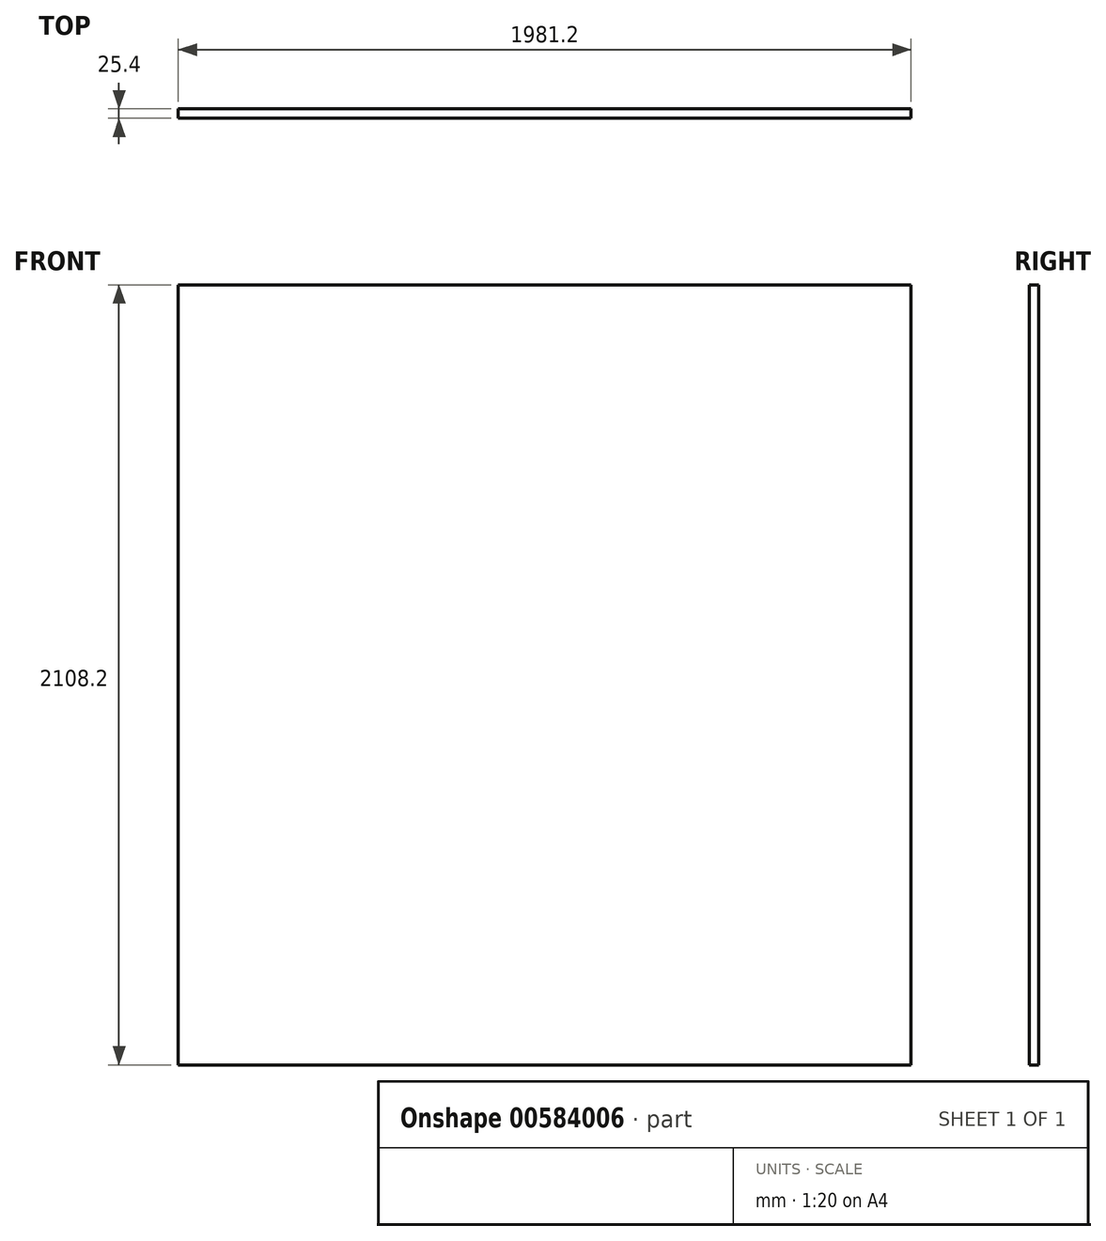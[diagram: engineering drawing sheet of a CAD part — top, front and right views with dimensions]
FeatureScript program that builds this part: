
annotation { "Feature Type Name" : "Feature", "Feature Type Description" : "" }
export const myFeature = defineFeature(function(context is Context, id is Id, definition is map)
    precondition{}
    {
        {
            var Q0;
            Q0=qCreatedBy(makeId("Front.planeOp"),FACE);
            var sketch = newSketch(context, id + "F0", { "sketchPlane" : qUnion([Q0])});
            skLineSegment(sketch, "E0.bottom", {"start": v(961.35, -896.76) * mm, "end": v(-1019.85, -896.76) * mm});
            skLineSegment(sketch, "E0.top", {"start": v(961.35, 1211.44) * mm, "end": v(-1019.85, 1211.44) * mm});
            skLineSegment(sketch, "E0.left", {"start": v(961.35, -896.76) * mm, "end": v(961.35, 1211.44) * mm});
            skLineSegment(sketch, "E0.right", {"start": v(-1019.85, -896.76) * mm, "end": v(-1019.85, 1211.44) * mm});
            skPoint(sketch, "E0.middle", {"position": v(-29.25, 157.34) * mm});
            skLineSegment(sketch, "E1", {"start": v(-1019.85, -871.36) * mm, "end": v(961.35, -871.36) * mm, "construction": true});
            skSolve(sketch);
        }
        {
            var Q0;
            Q0=makeQuery(id+"F0.imprint","IMPRINT",FACE,{"disambiguationData":[TD([[makeQuery(id+"F0.imprint","IMPRINT",EDGE,{"derivedFrom":sQuery(id+"F0.wireOp",EDGE,"E0.bottom")}),-1.0]])]});
            extrude(context, id + "F1", {"entities" : qUnion([Q0]), "depth" : 25.4 * mm, "offsetDistance" : 25.4 * mm});
        }
    });
